# Revit family: Shower_Arm-GROHE-Rainshower-28540_Series
name_source: partatom
category: Plumbing Fixtures
units: mm (PartAtom-declared; Revit-internal decimal feet)

## family parameters
Cut with Voids When Loaded = No
Host = Face
OmniClass Number = 23.45.05.14.17
OmniClass Title = Showers
Part Type = Normal
Room Calculation Point = No
Round Connector Dimension = Use Diameter
Shared = Yes

## types (5) — shared parameters
Assembly Code = D2090800
CW Connection = No
CWFU = 3
Default Elevation = 78"
Description = Rainshower®
Flow Rate = 2.0 gpm (7.6 L/min)
HW Connection = No
HWFU = 3
Height = 3 11/32"
IAPMO Compliance = CSA B125.1, ASME A112.18.1
Installation Type = Wall Mounted
Length = 15 3/16"
Manufacturer = Grohe
Price = Prices may vary. Please consult Manufacturer Representative for most up-to-date price list.
Product Documentation Link = https://americanstandard.box.com
Product Page URL = https://www.grohe.us
Revised Date = 04/26/2022
Tempered Connection Diameter = 1/2"
Tempered Connection Radius = 1/4"
Tempered Water Connection = Yes
URL = https://www.grohe.us
Vent Connection = No
WFU = 4
Warranty Documentation Link = https://cdn.cloud.grohe.com
Waste Connection = No
Width = 2 9/16"

## per-type parameters (varying)
| type | Finish | Material |
| 28540000 | Metal-Grohe-000-Chrome | Metal-Grohe-000-Chrome |
| 28540BE0 | Metal-Grohe-BE0-Nickel | Metal-Grohe-BE0-Nickel |
| 28540EN0 | Metal-Grohe-EN0-Brushed Nickel | Metal-Grohe-EN0-Brushed Nickel |
| 28540GN0 | Metal-Grohe-GN0-Brushed Cool Sunrise | Metal-Grohe-GN0-Brushed Cool Sunrise |
| 28540A00 | Metal-Grohe-A00-Hard Graphite | Metal-Grohe-A00-Hard Graphite |

note: column(s) folded — value = type name in every type: Model

## geometry (parser evidence)
native form markers: Sweep x3
no freeform markers — native parametric forms only
